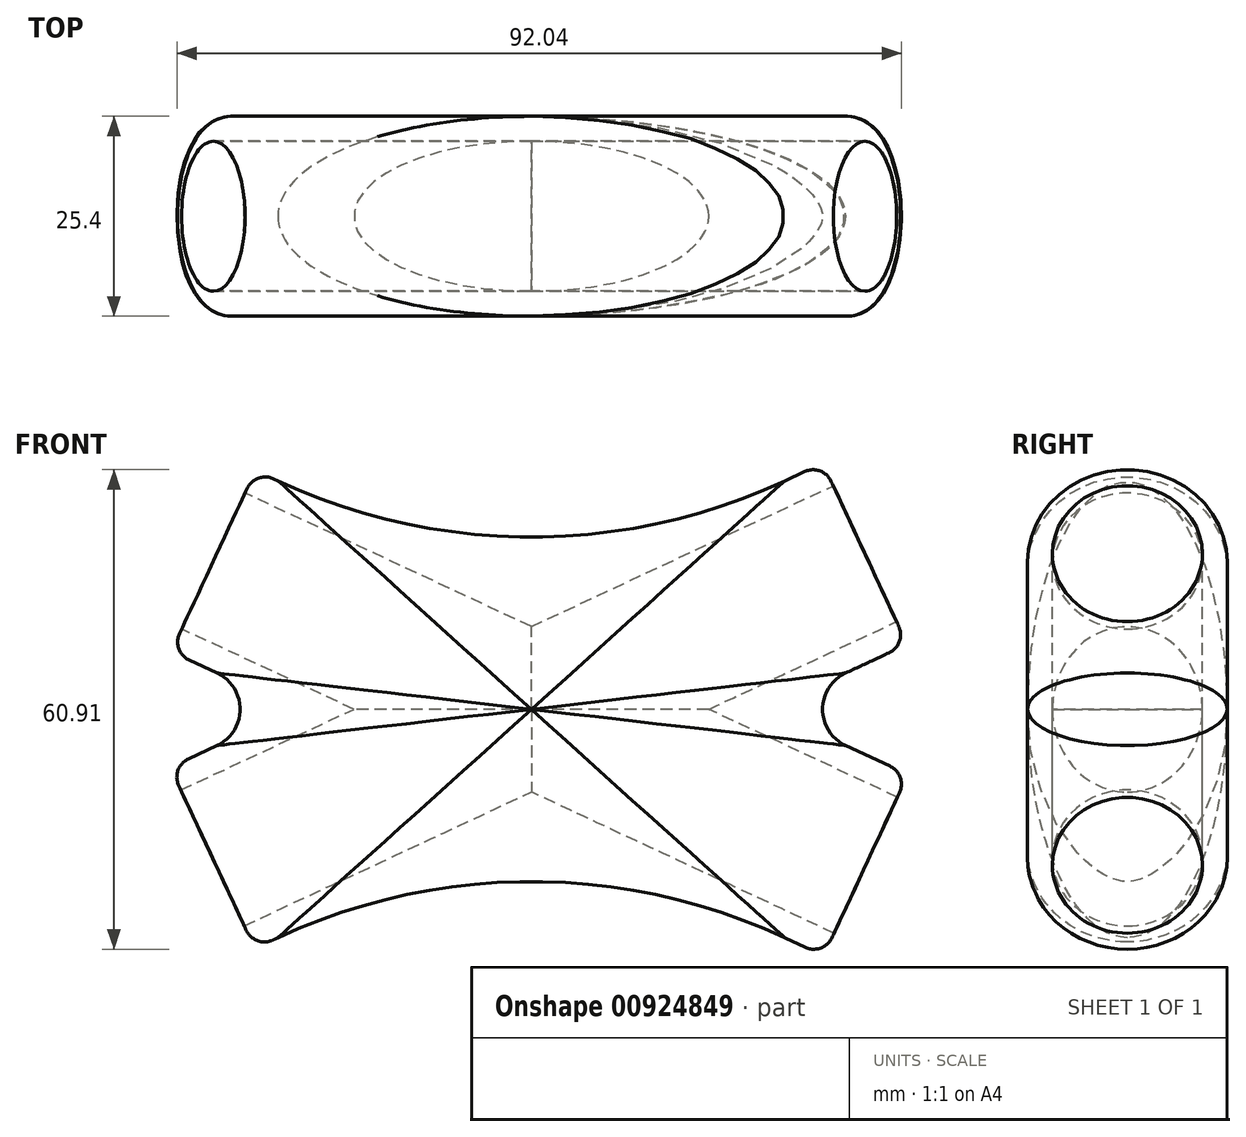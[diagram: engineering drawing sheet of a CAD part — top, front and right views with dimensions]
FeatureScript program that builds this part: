
annotation { "Feature Type Name" : "Feature", "Feature Type Description" : "" }
export const myFeature = defineFeature(function(context is Context, id is Id, definition is map)
    precondition{}
    {
        {
            var Q0;
            Q0=qCreatedBy(makeId("Right.planeOp"),FACE);
            var sketch = newSketch(context, id + "F0", { "sketchPlane" : qUnion([Q0])});
            skLineSegment(sketch, "E0", {"start": v(-76.37, 0) * mm, "end": v(76.06, 0) * mm});
            skSolve(sketch);
        }
        {
            var Q0;
            Q0=qCreatedBy(makeId("Right.planeOp"),FACE);
            var Q1;
            Q1=sQuery(id+"F0.wireOp",EDGE,"E0");
            cPlane(context, id + "F1", {"entities" : qUnion([Q0, Q1]), "cplaneType" : CPlaneType.LINE_ANGLE, "offset" : 25.4 * mm, "angle" : 65 * degree, "width" : 152.4 * mm, "height" : 152.4 * mm});
        }
        {
            var Q0;
            Q0=qCreatedBy(makeId("Right.planeOp"),FACE);
            var Q1;
            Q1=sQuery(id+"F0.wireOp",EDGE,"E0");
            cPlane(context, id + "F2", {"entities" : qUnion([Q0, Q1]), "cplaneType" : CPlaneType.LINE_ANGLE, "offset" : 25.4 * mm, "angle" : 65 * degree, "oppositeDirection" : true, "width" : 152.4 * mm, "height" : 152.4 * mm});
        }
        {
            var Q0;
            Q0=qCreatedBy(id+"F2.planeOp",FACE);
            var sketch = newSketch(context, id + "F3", { "sketchPlane" : qUnion([Q0])});
            skLineSegment(sketch, "E1", {"start": v(-69.97, 90.42) * mm, "end": v(-69.97, -91.18) * mm});
            skSolve(sketch);
        }
        {
            var Q0;
            Q0=qCreatedBy(id+"F1.planeOp",FACE);
            var sketch = newSketch(context, id + "F4", { "sketchPlane" : qUnion([Q0])});
            skLineSegment(sketch, "E2", {"start": v(72.15, 88.02) * mm, "end": v(72.15, -87.85) * mm});
            skSolve(sketch);
        }
        {
            var Q0;
            Q0=sQuery(id+"F3.wireOp",EDGE,"E1");
            var Q1;
            Q1=qCreatedBy(id+"F2.planeOp",FACE);
            cPlane(context, id + "F5", {"entities" : qUnion([Q0, Q1]), "cplaneType" : CPlaneType.LINE_ANGLE, "offset" : 25.4 * mm, "angle" : 90 * degree, "width" : 152.4 * mm, "height" : 152.4 * mm});
        }
        {
            var Q0;
            Q0=qCreatedBy(id+"F1.planeOp",FACE);
            var Q1;
            Q1=sQuery(id+"F4.wireOp",EDGE,"E2");
            cPlane(context, id + "F6", {"entities" : qUnion([Q0, Q1]), "cplaneType" : CPlaneType.LINE_ANGLE, "offset" : 25.4 * mm, "angle" : 90 * degree, "width" : 152.4 * mm, "height" : 152.4 * mm});
        }
        {
            var Q0;
            Q0=qCreatedBy(id+"F6.planeOp",FACE);
            var sketch = newSketch(context, id + "F7", { "sketchPlane" : qUnion([Q0])});
            skCircle(sketch, "E3", {"center": v(0, 0) * mm, "radius": 12.7 * mm});
            skCircle(sketch, "E4", {"center": v(0, 0) * mm, "radius": 9.52 * mm});
            skSolve(sketch);
        }
        {
            var Q0;
            Q0=qCreatedBy(id+"F5.planeOp",FACE);
            var sketch = newSketch(context, id + "F8", { "sketchPlane" : qUnion([Q0])});
            skCircle(sketch, "E5", {"center": v(0, 0) * mm, "radius": 12.7 * mm});
            skCircle(sketch, "E6", {"center": v(0, 0) * mm, "radius": 9.53 * mm});
            skSolve(sketch);
        }
        {
            var Q0;
            Q0=makeQuery(id+"F7.imprint","IMPRINT",FACE,{"disambiguationData":[TD([[makeQuery(id+"F7.imprint","IMPRINT",EDGE,{"derivedFrom":sQuery(id+"F7.wireOp",EDGE,"E3")}),1.0]])]});
            extrude(context, id + "F9", {"entities" : qUnion([Q0]), "oppositeDirection" : true, "depth" : 116.84 * mm, "offsetDistance" : 25.4 * mm, "hasSecondDirection" : true, "secondDirectionOppositeDirection" : true, "secondDirectionDepth" : 25.4 * mm});
        }
        {
            var Q0;
            Q0=makeQuery(id+"F8.imprint","IMPRINT",FACE,{"disambiguationData":[TD([[makeQuery(id+"F8.imprint","IMPRINT",EDGE,{"derivedFrom":sQuery(id+"F8.wireOp",EDGE,"E5")}),1.0]])]});
            extrude(context, id + "F10", {"entities" : qUnion([Q0]), "operationType" : NewBodyOperationType.ADD, "depth" : 116.84 * mm, "offsetDistance" : 25.4 * mm, "hasSecondDirection" : true, "secondDirectionOppositeDirection" : false, "secondDirectionDepth" : 25.4 * mm});
        }
        {
            var Q0;
            Q0=qCreatedBy(id+"F6.planeOp",FACE);
            var sketch = newSketch(context, id + "F11", { "sketchPlane" : qUnion([Q0])});
            skCircle(sketch, "E7", {"center": v(0, 0) * mm, "radius": 9.53 * mm});
            skSolve(sketch);
        }
        {
            var Q0;
            Q0 = qSketchRegion(id + "F11", true);
            extrude(context, id + "F12", {"entities" : qUnion([Q0]), "operationType" : NewBodyOperationType.REMOVE, "oppositeDirection" : true, "depth" : 156.46 * mm, "offsetDistance" : 25.4 * mm});
        }
        {
            var Q0;
            Q0=qCreatedBy(id+"F5.planeOp",FACE);
            var sketch = newSketch(context, id + "F13", { "sketchPlane" : qUnion([Q0])});
            skCircle(sketch, "E8", {"center": v(0, 0) * mm, "radius": 9.53 * mm});
            skSolve(sketch);
        }
        {
            var Q0;
            Q0 = qSketchRegion(id + "F13", true);
            extrude(context, id + "F14", {"entities" : qUnion([Q0]), "operationType" : NewBodyOperationType.REMOVE, "depth" : 176.53 * mm, "offsetDistance" : 25.4 * mm});
        }
        {
            var Q0;
            Q0=makeQuery(id+"F10.boolean.opBoolean","INTERSECT",EDGE,{"disambiguationData":[OD(2.0)],"derivedFrom":[makeQuery(id+"F9.opExtrude","SWEPT_FACE",FACE,{"disambiguationData":[OSD([sQuery(id+"F7.wireOp",EDGE,"E3")])]}),makeQuery(id+"F10.opExtrude","SWEPT_FACE",FACE,{"disambiguationData":[OSD([sQuery(id+"F8.wireOp",EDGE,"E5")])]})]});
            var Q1;
            Q1=makeQuery(id+"F10.boolean.opBoolean","INTERSECT",EDGE,{"disambiguationData":[OD(1.0)],"derivedFrom":[makeQuery(id+"F9.opExtrude","SWEPT_FACE",FACE,{"disambiguationData":[OSD([sQuery(id+"F7.wireOp",EDGE,"E3")])]}),makeQuery(id+"F10.opExtrude","SWEPT_FACE",FACE,{"disambiguationData":[OSD([sQuery(id+"F8.wireOp",EDGE,"E5")])]})]});
            fillet(context, id + "F15", {"entities" : qUnion([Q0, Q1]), "radius" : 5.08 * mm, "tangentPropagation" : true, "allowEdgeOverflow" : false});
        }
        {
            var Q0;
            Q0=makeQuery(id+"F10.boolean.opBoolean","INTERSECT",EDGE,{"disambiguationData":[OD(0.0)],"derivedFrom":[makeQuery(id+"F9.opExtrude","SWEPT_FACE",FACE,{"disambiguationData":[OSD([sQuery(id+"F7.wireOp",EDGE,"E3")])]}),makeQuery(id+"F10.opExtrude","SWEPT_FACE",FACE,{"disambiguationData":[OSD([sQuery(id+"F8.wireOp",EDGE,"E5")])]})]});
            var Q1;
            Q1=makeQuery(id+"F10.boolean.opBoolean","INTERSECT",EDGE,{"disambiguationData":[OD(3.0)],"derivedFrom":[makeQuery(id+"F9.opExtrude","SWEPT_FACE",FACE,{"disambiguationData":[OSD([sQuery(id+"F7.wireOp",EDGE,"E3")])]}),makeQuery(id+"F10.opExtrude","SWEPT_FACE",FACE,{"disambiguationData":[OSD([sQuery(id+"F8.wireOp",EDGE,"E5")])]})]});
            fillet(context, id + "F16", {"entities" : qUnion([Q0, Q1]), "radius" : 76.2 * mm, "tangentPropagation" : true, "allowEdgeOverflow" : false});
        }
        {
            var Q0;
            Q0=makeQuery(id+"F10.opExtrude","CAP_EDGE",EDGE,{"disambiguationData":[OSD([sQuery(id+"F8.wireOp",EDGE,"E5")])],"isStart":true});
            var Q1;
            Q1=makeQuery(id+"F9.opExtrude","CAP_EDGE",EDGE,{"disambiguationData":[OSD([sQuery(id+"F7.wireOp",EDGE,"E3")])],"isStart":false});
            var Q2;
            Q2=makeQuery(id+"F10.opExtrude","CAP_EDGE",EDGE,{"disambiguationData":[OSD([sQuery(id+"F8.wireOp",EDGE,"E5")])],"isStart":false});
            var Q3;
            Q3=makeQuery(id+"F9.opExtrude","CAP_EDGE",EDGE,{"disambiguationData":[OSD([sQuery(id+"F7.wireOp",EDGE,"E3")])],"isStart":true});
            fillet(context, id + "F17", {"entities" : qUnion([Q0, Q1, Q2, Q3]), "radius" : 2.54 * mm, "tangentPropagation" : true, "allowEdgeOverflow" : false});
        }
    });
